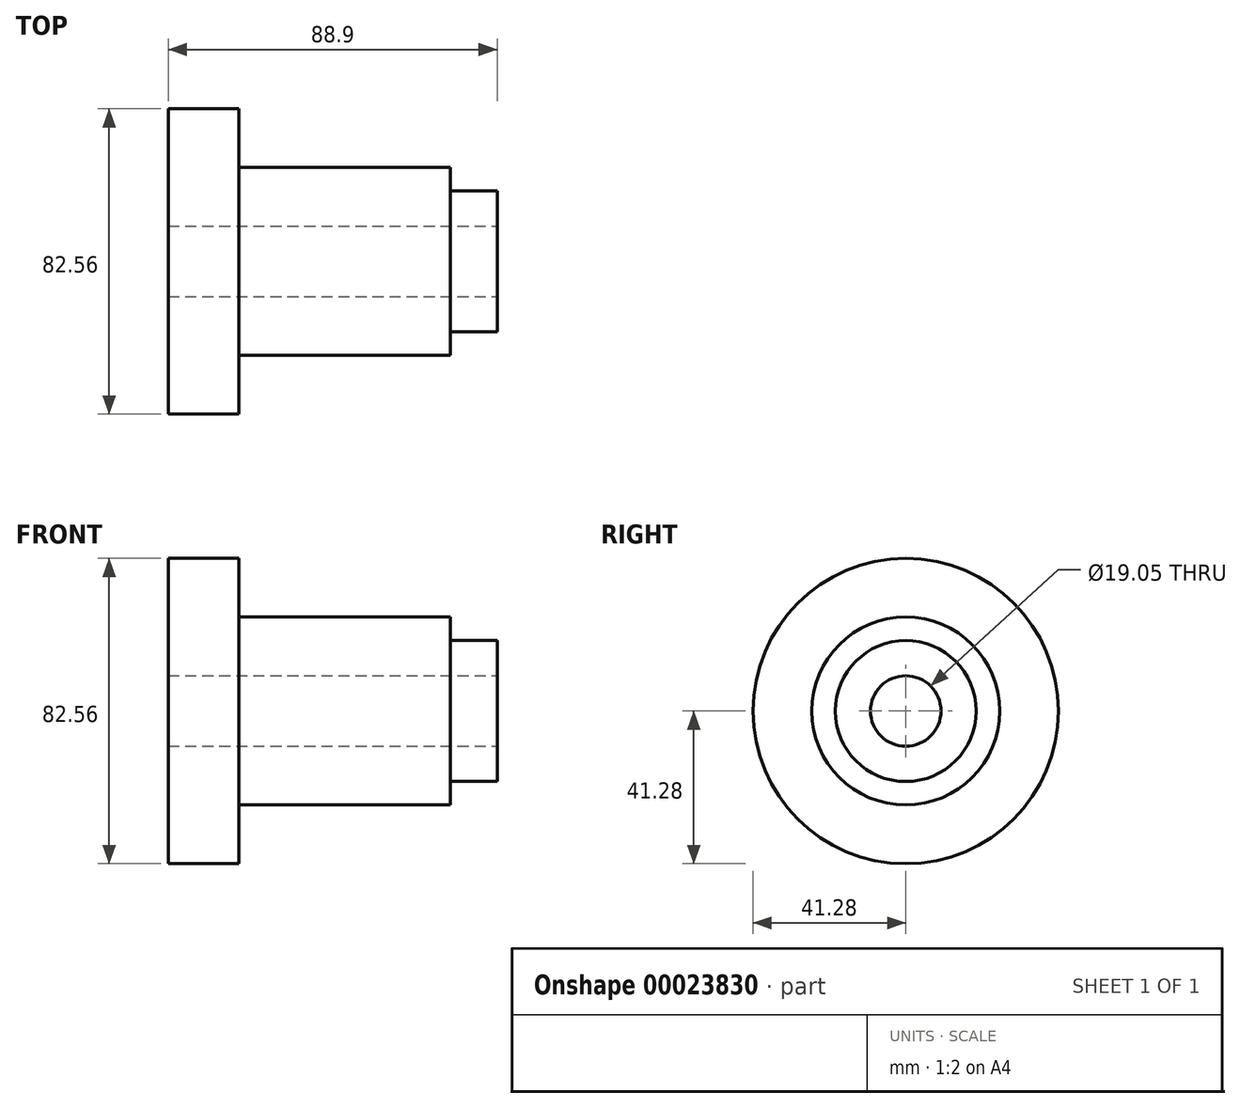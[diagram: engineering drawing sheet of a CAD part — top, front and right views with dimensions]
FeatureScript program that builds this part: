
annotation { "Feature Type Name" : "Feature", "Feature Type Description" : "" }
export const myFeature = defineFeature(function(context is Context, id is Id, definition is map)
    precondition{}
    {
        {
            var Q0;
            Q0=qCreatedBy(makeId("Front.planeOp"),FACE);
            var sketch = newSketch(context, id + "F0", { "sketchPlane" : qUnion([Q0])});
            skLineSegment(sketch, "E0", {"start": v(0, 0) * mm, "end": v(-100.6, 0) * mm, "construction": true});
            skLineSegment(sketch, "E1.bottom", {"start": v(0, 9.53) * mm, "end": v(-12.7, 9.53) * mm});
            skLineSegment(sketch, "E1.top", {"start": v(0, 19.05) * mm, "end": v(-12.7, 19.05) * mm});
            skLineSegment(sketch, "E1.left", {"start": v(0, 9.53) * mm, "end": v(0, 19.05) * mm});
            skLineSegment(sketch, "E1.right", {"start": v(-12.7, 9.53) * mm, "end": v(-12.7, 19.05) * mm});
            skLineSegment(sketch, "E2.bottom", {"start": v(-12.7, 9.53) * mm, "end": v(-69.85, 9.53) * mm});
            skLineSegment(sketch, "E2.top", {"start": v(-12.7, 25.4) * mm, "end": v(-69.85, 25.4) * mm});
            skLineSegment(sketch, "E2.left", {"start": v(-12.7, 9.53) * mm, "end": v(-12.7, 25.4) * mm});
            skLineSegment(sketch, "E2.right", {"start": v(-69.85, 9.52) * mm, "end": v(-69.85, 25.4) * mm});
            skLineSegment(sketch, "E3.bottom", {"start": v(-69.85, 9.53) * mm, "end": v(-88.9, 9.53) * mm});
            skLineSegment(sketch, "E3.top", {"start": v(-69.85, 41.27) * mm, "end": v(-88.9, 41.27) * mm});
            skLineSegment(sketch, "E3.left", {"start": v(-69.85, 9.52) * mm, "end": v(-69.85, 41.27) * mm});
            skLineSegment(sketch, "E3.right", {"start": v(-88.9, 9.52) * mm, "end": v(-88.9, 41.27) * mm});
            skSolve(sketch);
        }
        {
            var Q0;
            {var subQ3=sQuery(id+"F0.wireOp",EDGE,"E3.bottom");Q0=makeQuery(id+"F0.imprint","IMPRINT",FACE,{"disambiguationData":[TD([[makeQuery(id+"F0.imprint","IMPRINT",EDGE,{"derivedFrom":subQ3}),-1.0]])]});}
            var Q1;
            {var subQ2=sQuery(id+"F0.wireOp",EDGE,"E2.bottom");Q1=makeQuery(id+"F0.imprint","IMPRINT",FACE,{"disambiguationData":[TD([[makeQuery(id+"F0.imprint","IMPRINT",EDGE,{"derivedFrom":subQ2}),-1.0]])]});}
            var Q2;
            {var subQ2=sQuery(id+"F0.wireOp",EDGE,"E1.bottom");Q2=makeQuery(id+"F0.imprint","IMPRINT",FACE,{"disambiguationData":[TD([[makeQuery(id+"F0.imprint","IMPRINT",EDGE,{"derivedFrom":subQ2}),-1.0]])]});}
            var Q3;
            Q3=sQuery(id+"F0.wireOp",EDGE,"E0");
            revolve(context, id + "F1", {"entities" : qUnion([Q0, Q1, Q2]), "axis" : qUnion([Q3]), "revolveType" : RevolveType.FULL});
        }
    });
